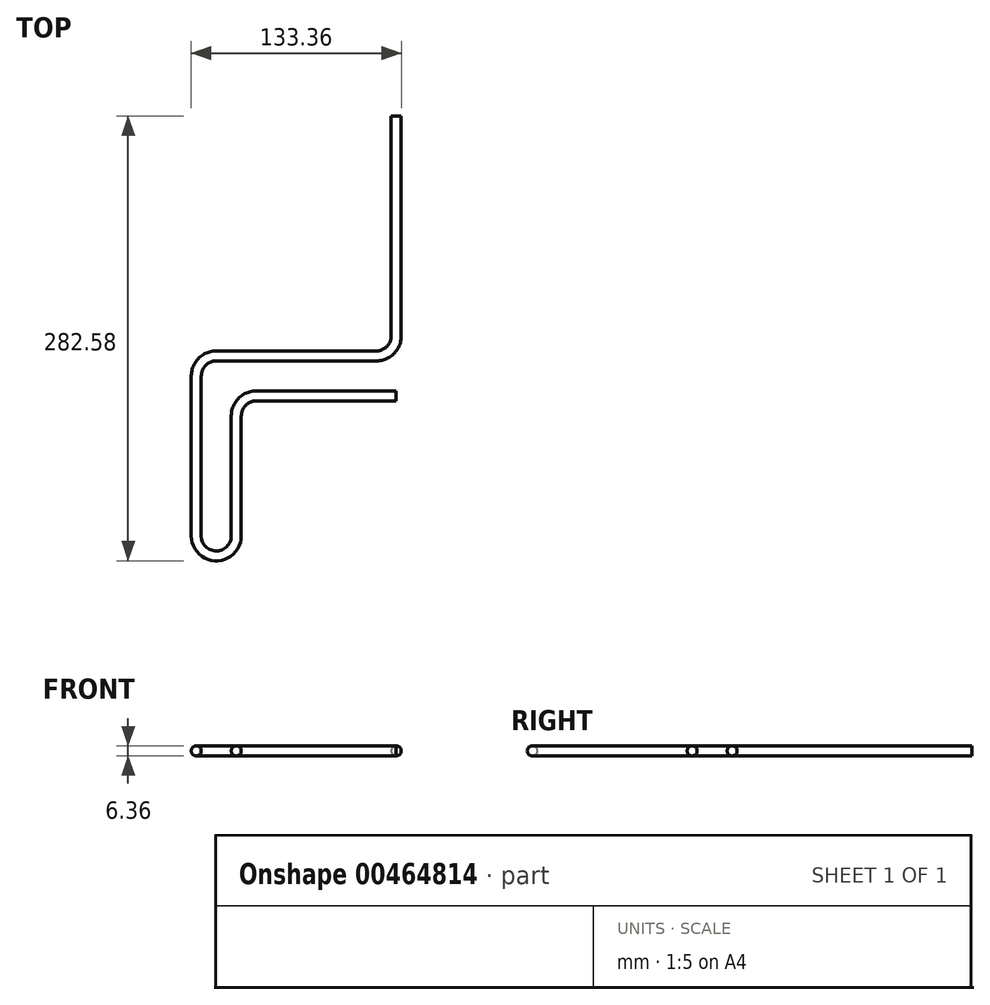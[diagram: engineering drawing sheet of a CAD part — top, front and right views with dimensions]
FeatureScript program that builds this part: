
annotation { "Feature Type Name" : "Feature", "Feature Type Description" : "" }
export const myFeature = defineFeature(function(context is Context, id is Id, definition is map)
    precondition{}
    {
        {
            var Q0;
            Q0=qCreatedBy(makeId("Top.planeOp"),FACE);
            var sketch = newSketch(context, id + "F0", { "sketchPlane" : qUnion([Q0])});
            skLineSegment(sketch, "E0", {"start": v(0, -12.7) * mm, "end": v(0, -114.3) * mm});
            skLineSegment(sketch, "E1", {"start": v(0, -114.3) * mm, "end": v(25.4, -114.3) * mm, "construction": true});
            skLineSegment(sketch, "E2", {"start": v(25.4, -114.3) * mm, "end": v(25.4, -38.1) * mm});
            skLineSegment(sketch, "E3", {"start": v(38.1, -25.4) * mm, "end": v(127, -25.4) * mm});
            skLineSegment(sketch, "E4", {"start": v(12.7, 0) * mm, "end": v(114.3, 0) * mm});
            skLineSegment(sketch, "E5", {"start": v(127, 12.7) * mm, "end": v(127, 152.4) * mm});
            skLineSegment(sketch, "E6", {"start": v(127, 0) * mm, "end": v(127, -25.4) * mm, "construction": true});
            skArc(sketch, "E7", {"start": v(0, -114.3) * mm, "mid": v(12.7, -127) * mm, "end": v(25.4, -114.3) * mm});
            skPoint(sketch, "E8.visualSharp", {"position": v(0, 0) * mm});
            skArc(sketch, "E8.filletArc", {"start": v(12.7, 0) * mm, "mid": v(3.72, -3.72) * mm, "end": v(0, -12.7) * mm});
            skPoint(sketch, "E9.visualSharp", {"position": v(25.4, -25.4) * mm});
            skArc(sketch, "E9.filletArc", {"start": v(38.1, -25.4) * mm, "mid": v(29.12, -29.12) * mm, "end": v(25.4, -38.1) * mm});
            skPoint(sketch, "E10.visualSharp", {"position": v(127, 0) * mm});
            skArc(sketch, "E10.filletArc", {"start": v(114.3, 0) * mm, "mid": v(123.28, 3.72) * mm, "end": v(127, 12.7) * mm});
            skSolve(sketch);
        }
        {
            var Q0;
            Q0=qCreatedBy(makeId("Front.planeOp"),FACE);
            cPlane(context, id + "F1", {"entities" : qUnion([Q0]), "cplaneType" : CPlaneType.OFFSET, "offset" : 152.4 * mm, "oppositeDirection" : true, "width" : 152.4 * mm, "height" : 152.4 * mm});
        }
        {
            var Q0;
            Q0=qCreatedBy(id+"F1.planeOp",FACE);
            var sketch = newSketch(context, id + "F2", { "sketchPlane" : qUnion([Q0])});
            skCircle(sketch, "E11", {"center": v(127, 0) * mm, "radius": 3.18 * mm});
            skSolve(sketch);
        }
        {
            var Q0;
            Q0=makeQuery(id+"F2.imprint","IMPRINT",FACE,{"disambiguationData":[TD([[makeQuery(id+"F2.imprint","IMPRINT",EDGE,{"derivedFrom":sQuery(id+"F2.wireOp",EDGE,"E11")}),1.0]])]});
            var Q1;
            Q1=sQuery(id+"F0.wireOp",EDGE,"E5");
            var Q2;
            Q2=sQuery(id+"F0.wireOp",EDGE,"E10.filletArc");
            var Q3;
            Q3=sQuery(id+"F0.wireOp",EDGE,"E4");
            var Q4;
            Q4=sQuery(id+"F0.wireOp",EDGE,"E8.filletArc");
            var Q5;
            Q5=sQuery(id+"F0.wireOp",EDGE,"E0");
            var Q6;
            Q6=sQuery(id+"F0.wireOp",EDGE,"E7");
            var Q7;
            Q7=sQuery(id+"F0.wireOp",EDGE,"E2");
            var Q8;
            Q8=sQuery(id+"F0.wireOp",EDGE,"E9.filletArc");
            var Q9;
            Q9=sQuery(id+"F0.wireOp",EDGE,"E3");
            sweep(context, id + "F3", {"profiles" : qUnion([Q0]), "path" : qUnion([Q1, Q2, Q3, Q4, Q5, Q6, Q7, Q8, Q9])});
        }
    });
